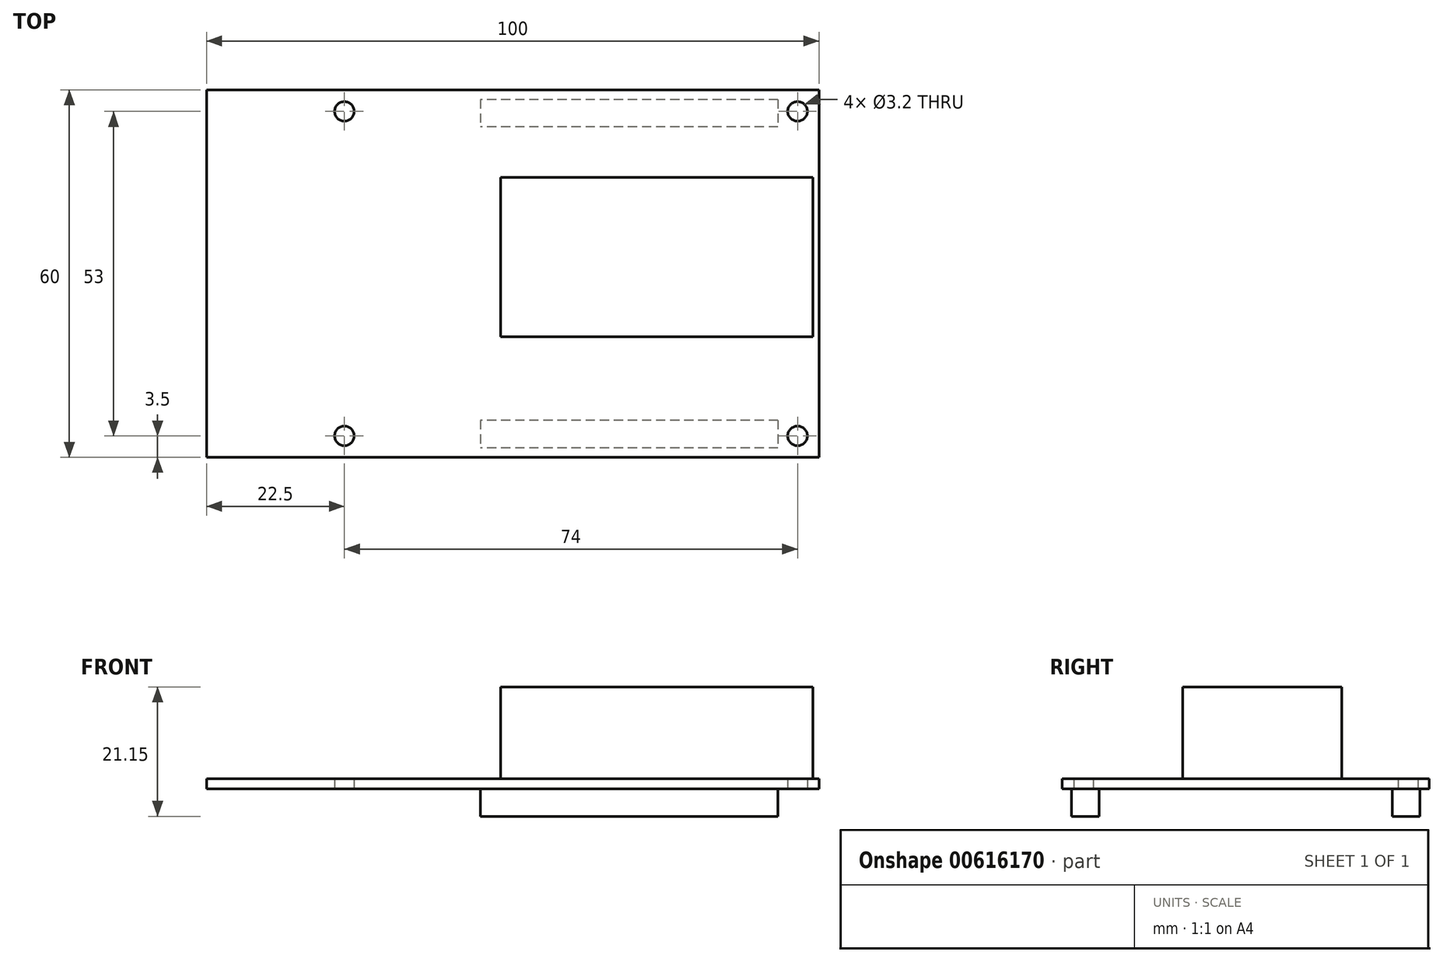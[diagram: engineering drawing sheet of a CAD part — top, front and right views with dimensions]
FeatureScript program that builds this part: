
annotation { "Feature Type Name" : "Feature", "Feature Type Description" : "" }
export const myFeature = defineFeature(function(context is Context, id is Id, definition is map)
    precondition{}
    {
        {
            var Q0;
            Q0=qCreatedBy(makeId("Top.planeOp"),FACE);
            var sketch = newSketch(context, id + "F0", { "sketchPlane" : qUnion([Q0])});
            skLineSegment(sketch, "E0.bottom", {"start": v(50, -30) * mm, "end": v(-50, -30) * mm});
            skLineSegment(sketch, "E0.top", {"start": v(50, 30) * mm, "end": v(-50, 30) * mm});
            skLineSegment(sketch, "E0.left", {"start": v(50, -30) * mm, "end": v(50, 30) * mm});
            skLineSegment(sketch, "E0.right", {"start": v(-50, -30) * mm, "end": v(-50, 30) * mm});
            skPoint(sketch, "E0.middle", {"position": v(0, 0) * mm});
            skCircle(sketch, "E1", {"center": v(46.5, 26.5) * mm, "radius": 1.6 * mm});
            skCircle(sketch, "E2", {"center": v(46.5, -26.5) * mm, "radius": 1.6 * mm});
            skCircle(sketch, "E3", {"center": v(-27.5, -26.5) * mm, "radius": 1.6 * mm});
            skCircle(sketch, "E4", {"center": v(-27.5, 26.5) * mm, "radius": 1.6 * mm});
            skLineSegment(sketch, "E5", {"start": v(46.5, 48.23) * mm, "end": v(46.5, -51.59) * mm, "construction": true});
            skLineSegment(sketch, "E6", {"start": v(63.05, -26.5) * mm, "end": v(-67.21, -26.5) * mm, "construction": true});
            skLineSegment(sketch, "E7", {"start": v(47.64, 26.5) * mm, "end": v(-91.9, 26.5) * mm, "construction": true});
            skLineSegment(sketch, "E8", {"start": v(-27.5, 41.98) * mm, "end": v(-27.5, -42.14) * mm, "construction": true});
            skSolve(sketch);
        }
        {
            var Q0;
            Q0=makeQuery(id+"F0.imprint","IMPRINT",FACE,{"disambiguationData":[TD([[makeQuery(id+"F0.imprint","IMPRINT",EDGE,{"derivedFrom":sQuery(id+"F0.wireOp",EDGE,"E0.bottom")}),-1.0]])]});
            extrude(context, id + "F1", {"entities" : qUnion([Q0]), "depth" : 1.65 * mm, "offsetDistance" : 25 * mm});
        }
        {
            var Q0;
            Q0=makeQuery(id+"F1.opExtrude","CAP_FACE",FACE,{"disambiguationData":[OSD([sQuery(id+"F0.wireOp",EDGE,"E0.bottom"),sQuery(id+"F0.wireOp",EDGE,"E0.top"),sQuery(id+"F0.wireOp",EDGE,"E0.left"),sQuery(id+"F0.wireOp",EDGE,"E0.right"),sQuery(id+"F0.wireOp",EDGE,"E1"),sQuery(id+"F0.wireOp",EDGE,"E2"),sQuery(id+"F0.wireOp",EDGE,"E3"),sQuery(id+"F0.wireOp",EDGE,"E4")])],"isStart":true});
            var sketch = newSketch(context, id + "F2", { "sketchPlane" : qUnion([Q0])});
            skLineSegment(sketch, "E9.bottom", {"start": v(43.3, 23.95) * mm, "end": v(-5.3, 23.95) * mm});
            skLineSegment(sketch, "E9.top", {"start": v(43.3, 28.45) * mm, "end": v(-5.3, 28.45) * mm});
            skLineSegment(sketch, "E9.left", {"start": v(43.3, 23.95) * mm, "end": v(43.3, 28.45) * mm});
            skLineSegment(sketch, "E9.right", {"start": v(-5.3, 23.95) * mm, "end": v(-5.3, 28.45) * mm});
            skPoint(sketch, "E9.middle", {"position": v(19, 26.2) * mm});
            skLineSegment(sketch, "E10", {"start": v(19, 29.56) * mm, "end": v(19, -51.84) * mm, "construction": true});
            skLineSegment(sketch, "E11.bottom", {"start": v(43.3, -28.45) * mm, "end": v(-5.3, -28.45) * mm});
            skLineSegment(sketch, "E11.top", {"start": v(43.3, -23.95) * mm, "end": v(-5.3, -23.95) * mm});
            skLineSegment(sketch, "E11.left", {"start": v(43.3, -28.45) * mm, "end": v(43.3, -23.95) * mm});
            skLineSegment(sketch, "E11.right", {"start": v(-5.3, -28.45) * mm, "end": v(-5.3, -23.95) * mm});
            skPoint(sketch, "E11.middle", {"position": v(19, -26.2) * mm});
            skSolve(sketch);
        }
        {
            var Q0;
            Q0=makeQuery(id+"F2.imprint","IMPRINT",FACE,{"disambiguationData":[TD([[makeQuery(id+"F2.imprint","IMPRINT",EDGE,{"derivedFrom":sQuery(id+"F2.wireOp",EDGE,"E9.bottom")}),-1.0]])]});
            var Q1;
            Q1=makeQuery(id+"F2.imprint","IMPRINT",FACE,{"disambiguationData":[TD([[makeQuery(id+"F2.imprint","IMPRINT",EDGE,{"derivedFrom":sQuery(id+"F2.wireOp",EDGE,"E11.bottom")}),-1.0]])]});
            extrude(context, id + "F3", {"entities" : qUnion([Q0, Q1]), "operationType" : NewBodyOperationType.ADD, "depth" : 4.5 * mm, "offsetDistance" : 25 * mm});
        }
        {
            var Q0;
            Q0=makeQuery(id+"F1.opExtrude","CAP_FACE",FACE,{"disambiguationData":[OSD([sQuery(id+"F0.wireOp",EDGE,"E0.bottom"),sQuery(id+"F0.wireOp",EDGE,"E0.top"),sQuery(id+"F0.wireOp",EDGE,"E0.left"),sQuery(id+"F0.wireOp",EDGE,"E0.right"),sQuery(id+"F0.wireOp",EDGE,"E1"),sQuery(id+"F0.wireOp",EDGE,"E2"),sQuery(id+"F0.wireOp",EDGE,"E3"),sQuery(id+"F0.wireOp",EDGE,"E4")])],"isStart":false});
            var sketch = newSketch(context, id + "F4", { "sketchPlane" : qUnion([Q0])});
            skLineSegment(sketch, "E12.bottom", {"start": v(-2, 15.7) * mm, "end": v(49, 15.7) * mm});
            skLineSegment(sketch, "E12.top", {"start": v(-2, -10.3) * mm, "end": v(49, -10.3) * mm});
            skLineSegment(sketch, "E12.left", {"start": v(-2, 15.7) * mm, "end": v(-2, -10.3) * mm});
            skLineSegment(sketch, "E12.right", {"start": v(49, 15.7) * mm, "end": v(49, -10.3) * mm});
            skSolve(sketch);
        }
        {
            var Q0;
            Q0=makeQuery(id+"F4.imprint","IMPRINT",FACE,{"disambiguationData":[TD([[makeQuery(id+"F4.imprint","IMPRINT",EDGE,{"derivedFrom":sQuery(id+"F4.wireOp",EDGE,"E12.bottom")}),-1.0]])]});
            extrude(context, id + "F5", {"entities" : qUnion([Q0]), "operationType" : NewBodyOperationType.ADD, "depth" : 15 * mm, "offsetDistance" : 25 * mm});
        }
    });
